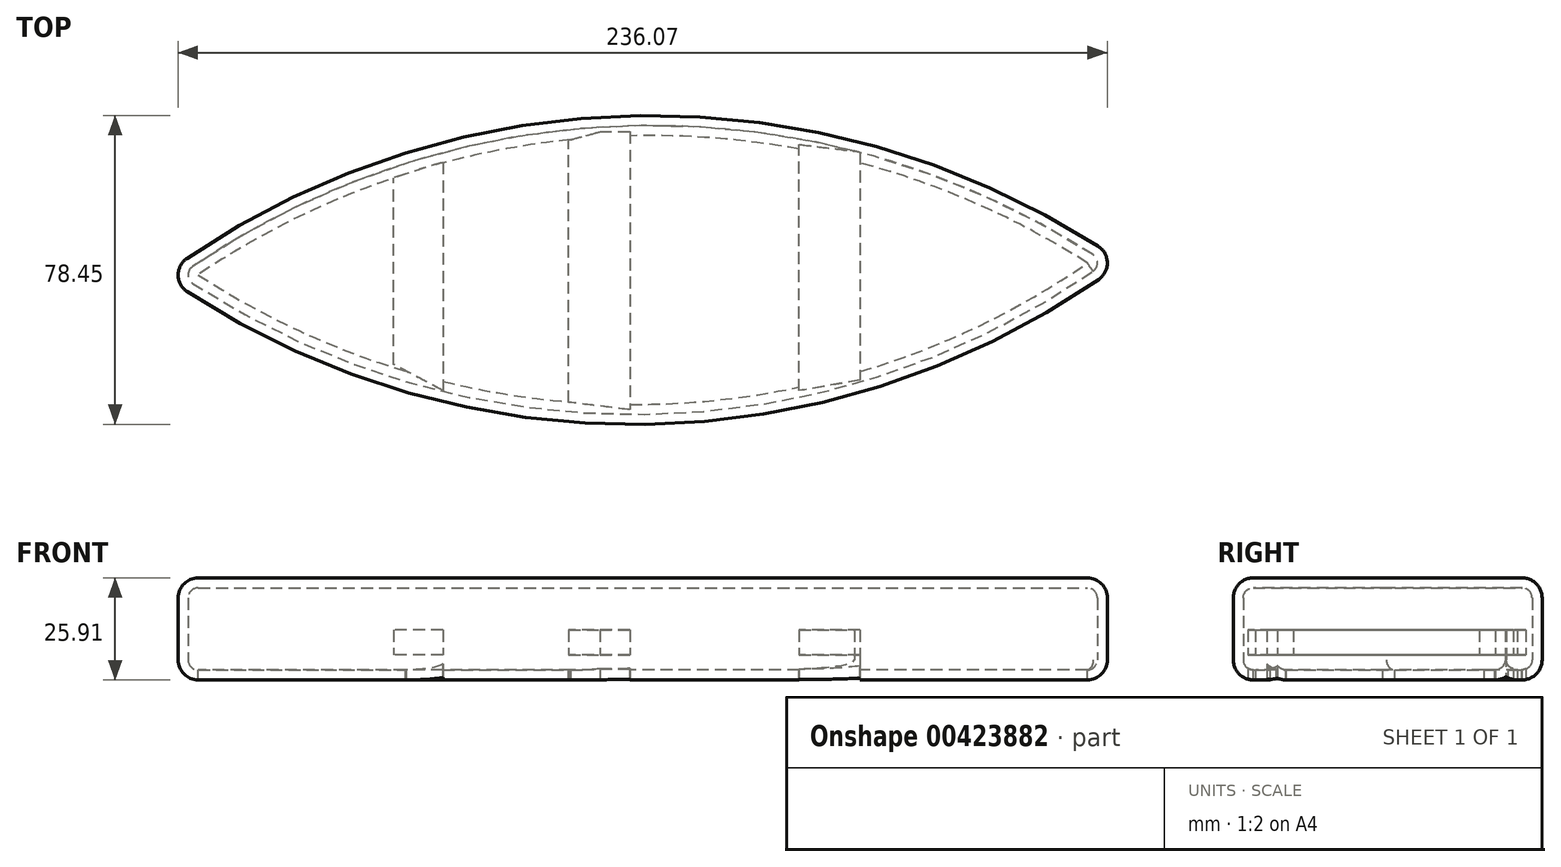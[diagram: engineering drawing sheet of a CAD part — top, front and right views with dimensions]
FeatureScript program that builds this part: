
annotation { "Feature Type Name" : "Feature", "Feature Type Description" : "" }
export const myFeature = defineFeature(function(context is Context, id is Id, definition is map)
    precondition{}
    {
        {
            var Q0;
            Q0=qCreatedBy(makeId("Top.planeOp"),FACE);
            var sketch = newSketch(context, id + "F0", { "sketchPlane" : qUnion([Q0])});
            skArc(sketch, "E0", {"start": v(132.75, -16.55) * mm, "mid": v(10.34, 20.73) * mm, "end": v(-111.04, -19.8) * mm});
            skArc(sketch, "E1", {"start": v(-111.04, -19.8) * mm, "mid": v(11.38, -57.69) * mm, "end": v(132.75, -16.55) * mm});
            skSolve(sketch);
        }
        {
            var Q0;
            Q0=makeQuery(id+"F0.imprint","IMPRINT",FACE,{"disambiguationData":[TD([[makeQuery(id+"F0.imprint","IMPRINT",EDGE,{"derivedFrom":sQuery(id+"F0.wireOp",EDGE,"E0")}),1.0]])]});
            extrude(context, id + "F1", {"entities" : qUnion([Q0]), "depth" : 25.9 * mm});
        }
        {
            var Q0;
            Q0=makeQuery(id+"F1.opExtrude","SWEPT_FACE",FACE,{"disambiguationData":[OSD([sQuery(id+"F0.wireOp",EDGE,"E1")])]});
            var Q1;
            Q1=makeQuery(id+"F1.opExtrude","CAP_FACE",FACE,{"disambiguationData":[OSD([sQuery(id+"F0.wireOp",EDGE,"E0"),sQuery(id+"F0.wireOp",EDGE,"E1")])],"isStart":true});
            var Q2;
            Q2=makeQuery(id+"F1.opExtrude","SWEPT_FACE",FACE,{"disambiguationData":[OSD([sQuery(id+"F0.wireOp",EDGE,"E0")])]});
            var Q3;
            Q3=makeQuery(id+"F1.opExtrude","CAP_FACE",FACE,{"disambiguationData":[OSD([sQuery(id+"F0.wireOp",EDGE,"E0"),sQuery(id+"F0.wireOp",EDGE,"E1")])],"isStart":false});
            fillet(context, id + "F2", {"entities" : qUnion([Q0, Q1, Q2, Q3]), "radius" : 5.08 * mm, "tangentPropagation" : true, "allowEdgeOverflow" : false});
        }
        {
            var Q0;
            Q0=makeQuery(id+"F1.opExtrude","CAP_FACE",FACE,{"disambiguationData":[OSD([sQuery(id+"F0.wireOp",EDGE,"E0"),sQuery(id+"F0.wireOp",EDGE,"E1")])],"isStart":true});
            shell(context, id + "F3", {"entities" : qUnion([Q0]), "thickness" : 2.54 * mm});
        }
        {
            var Q0;
            Q0=qCreatedBy(makeId("Top.planeOp"),FACE);
            var sketch = newSketch(context, id + "F4", { "sketchPlane" : qUnion([Q0])});
            skLineSegment(sketch, "E2", {"start": v(-52.5, -42.42) * mm, "end": v(-52.5, 4.83) * mm});
            skArc(sketch, "E3", {"start": v(-39.89, 8.86) * mm, "mid": v(-46.23, 6.96) * mm, "end": v(-52.5, 4.83) * mm});
            skLineSegment(sketch, "E4", {"start": v(-39.89, 8.86) * mm, "end": v(-39.89, -46.18) * mm});
            skLineSegment(sketch, "E5", {"start": v(-39.89, -46.18) * mm, "end": v(-39.89, -49.13) * mm});
            skLineSegment(sketch, "E6", {"start": v(-39.89, -49.13) * mm, "end": v(-52.5, -42.42) * mm});
            skLineSegment(sketch, "E7", {"start": v(-7.94, -52.09) * mm, "end": v(-7.94, 14.5) * mm});
            skLineSegment(sketch, "E8", {"start": v(-7.94, 14.5) * mm, "end": v(0, 16.65) * mm});
            skLineSegment(sketch, "E9", {"start": v(0, 16.65) * mm, "end": v(7.64, 16.65) * mm});
            skLineSegment(sketch, "E10", {"start": v(7.64, 16.65) * mm, "end": v(7.64, -53.97) * mm});
            skLineSegment(sketch, "E11", {"start": v(7.64, -53.97) * mm, "end": v(-7.94, -52.09) * mm});
            skLineSegment(sketch, "E12", {"start": v(50.6, -49.13) * mm, "end": v(50.6, 13.42) * mm});
            skLineSegment(sketch, "E13", {"start": v(50.6, 13.42) * mm, "end": v(66.06, 11.56) * mm});
            skLineSegment(sketch, "E14", {"start": v(66.06, 11.56) * mm, "end": v(66.06, -46.45) * mm});
            skLineSegment(sketch, "E15", {"start": v(66.06, -46.45) * mm, "end": v(50.6, -49.13) * mm});
            skSolve(sketch);
        }
        {
            var Q0;
            Q0 = qSketchRegion(id + "F4", true);
            extrude(context, id + "F5", {"entities" : qUnion([Q0]), "operationType" : NewBodyOperationType.ADD, "depth" : 12.7 * mm});
        }
        {
            var Q0;
            Q0=makeQuery(id+"F5.opExtrude","CAP_FACE",FACE,{"disambiguationData":[OSD([sQuery(id+"F4.wireOp",EDGE,"E12"),sQuery(id+"F4.wireOp",EDGE,"E13"),sQuery(id+"F4.wireOp",EDGE,"E14"),sQuery(id+"F4.wireOp",EDGE,"E15")])],"isStart":true});
            var Q1;
            Q1=makeQuery(id+"F5.opExtrude","CAP_FACE",FACE,{"disambiguationData":[OSD([sQuery(id+"F4.wireOp",EDGE,"E7"),sQuery(id+"F4.wireOp",EDGE,"E8"),sQuery(id+"F4.wireOp",EDGE,"E9"),sQuery(id+"F4.wireOp",EDGE,"E10"),sQuery(id+"F4.wireOp",EDGE,"E11")])],"isStart":true});
            var Q2;
            Q2=makeQuery(id+"F5.opExtrude","CAP_FACE",FACE,{"disambiguationData":[OSD([sQuery(id+"F4.wireOp",EDGE,"E2"),sQuery(id+"F4.wireOp",EDGE,"E3"),sQuery(id+"F4.wireOp",EDGE,"E4"),sQuery(id+"F4.wireOp",EDGE,"E5"),sQuery(id+"F4.wireOp",EDGE,"E6")])],"isStart":true});
            extrude(context, id + "F6", {"entities" : qUnion([Q0, Q1, Q2]), "operationType" : NewBodyOperationType.REMOVE, "oppositeDirection" : true, "depth" : 6.35 * mm});
        }
    });
